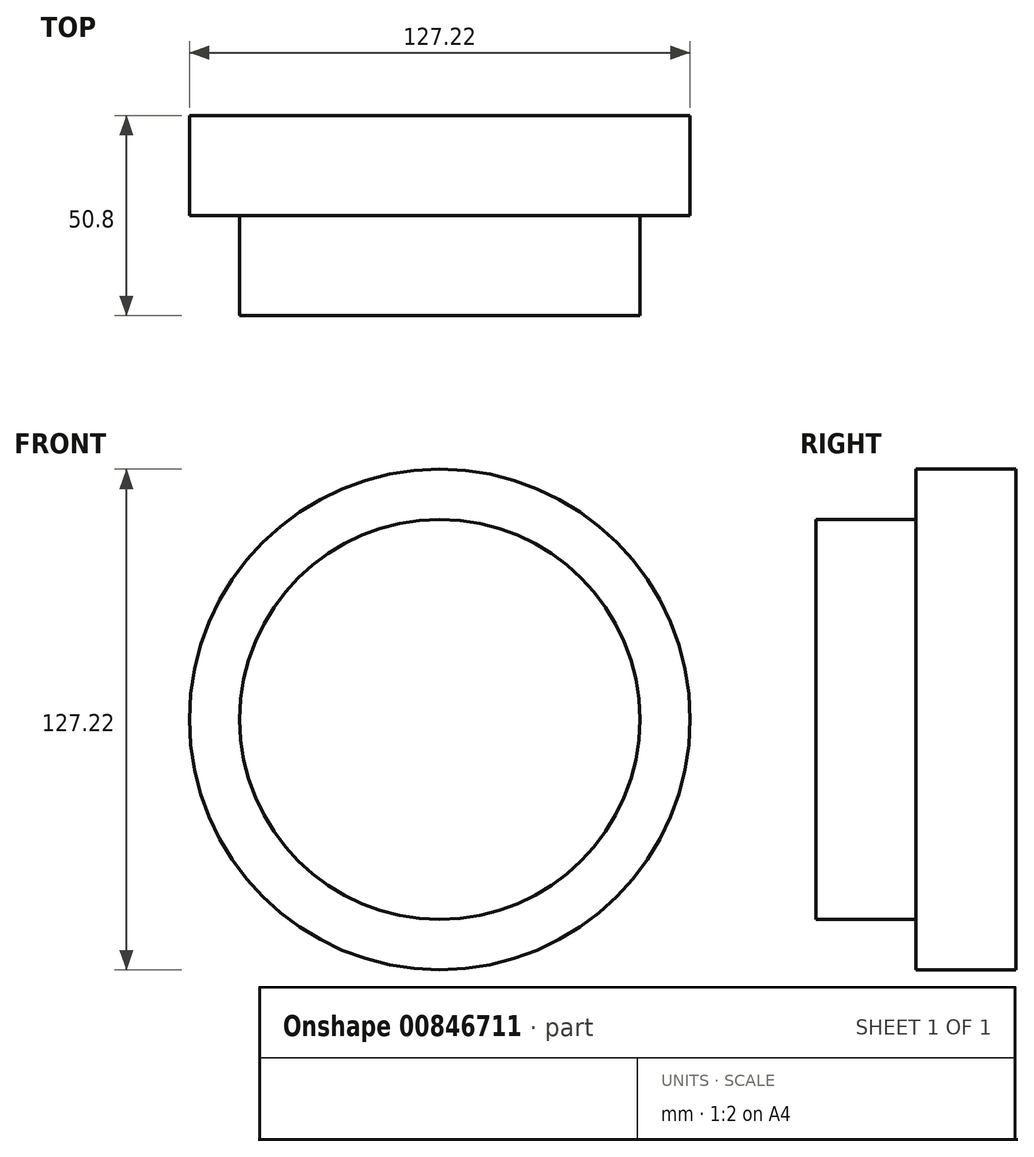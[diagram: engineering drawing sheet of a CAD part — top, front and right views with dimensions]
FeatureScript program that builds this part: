
annotation { "Feature Type Name" : "Feature", "Feature Type Description" : "" }
export const myFeature = defineFeature(function(context is Context, id is Id, definition is map)
    precondition{}
    {
        {
            var Q0;
            Q0=qCreatedBy(makeId("Front.planeOp"),FACE);
            var sketch = newSketch(context, id + "F0", { "sketchPlane" : qUnion([Q0])});
            skCircle(sketch, "E0", {"center": v(0, 0) * mm, "radius": 63.61 * mm});
            skSolve(sketch);
        }
        {
            var Q0;
            Q0=makeQuery(id+"F0.imprint","IMPRINT",FACE,{"disambiguationData":[TD([[makeQuery(id+"F0.imprint","IMPRINT",EDGE,{"derivedFrom":sQuery(id+"F0.wireOp",EDGE,"E0")}),1.0]])]});
            var sketch = newSketch(context, id + "F1", { "sketchPlane" : qUnion([Q0])});
            skCircle(sketch, "E1", {"center": v(0, 0) * mm, "radius": 32.02 * mm});
            skSolve(sketch);
        }
        {
            var Q0;
            Q0=makeQuery(id+"F0.imprint","IMPRINT",FACE,{"disambiguationData":[TD([[makeQuery(id+"F0.imprint","IMPRINT",EDGE,{"derivedFrom":sQuery(id+"F0.wireOp",EDGE,"E0")}),1.0]])]});
            var sketch = newSketch(context, id + "F2", { "sketchPlane" : qUnion([Q0])});
            skLineSegment(sketch, "E2.bottom", {"start": v(-12.32, 12.89) * mm, "end": v(12.7, 12.89) * mm});
            skLineSegment(sketch, "E2.top", {"start": v(-12.32, -14.6) * mm, "end": v(12.7, -14.6) * mm});
            skLineSegment(sketch, "E2.left", {"start": v(-12.32, 12.89) * mm, "end": v(-12.32, -14.6) * mm});
            skLineSegment(sketch, "E2.right", {"start": v(12.7, 12.89) * mm, "end": v(12.7, -14.6) * mm});
            skSolve(sketch);
        }
        {
            var Q0;
            Q0 = qSketchRegion(id + "F2", true);
            extrude(context, id + "F3", {"entities" : qUnion([Q0]), "depth" : 25.4 * mm, "offsetDistance" : 25.4 * mm});
        }
        {
            var Q0;
            Q0=makeQuery(id+"F0.imprint","IMPRINT",FACE,{"disambiguationData":[TD([[makeQuery(id+"F0.imprint","IMPRINT",EDGE,{"derivedFrom":sQuery(id+"F0.wireOp",EDGE,"E0")}),1.0]])]});
            var Q1;
            Q1=makeQuery(id+"F1.imprint","IMPRINT",FACE,{"disambiguationData":[TD([[makeQuery(id+"F1.imprint","IMPRINT",EDGE,{"derivedFrom":sQuery(id+"F1.wireOp",EDGE,"E1")}),1.0]])]});
            extrude(context, id + "F4", {"entities" : qUnion([Q0, Q1]), "operationType" : NewBodyOperationType.ADD, "depth" : 25.4 * mm, "offsetDistance" : 25.4 * mm});
        }
        {
            var Q0;
            Q0=makeQuery(id+"F4.boolean.opBoolean","MERGE",FACE,{"derivedFrom":[makeQuery(id+"F3.opExtrude","CAP_FACE",FACE,{"disambiguationData":[OSD([sQuery(id+"F2.wireOp",EDGE,"E2.bottom"),sQuery(id+"F2.wireOp",EDGE,"E2.top"),sQuery(id+"F2.wireOp",EDGE,"E2.left"),sQuery(id+"F2.wireOp",EDGE,"E2.right")])],"isStart":false}),makeQuery(id+"F4.opExtrude","CAP_FACE",FACE,{"disambiguationData":[OSD([sQuery(id+"F0.wireOp",EDGE,"E0")])],"isStart":false})]});
            var sketch = newSketch(context, id + "F5", { "sketchPlane" : qUnion([Q0])});
            skCircle(sketch, "E3", {"center": v(0, 0) * mm, "radius": 50.83 * mm});
            skSolve(sketch);
        }
        {
            var Q0;
            Q0=makeQuery(id+"F5.imprint","IMPRINT",FACE,{"disambiguationData":[TD([[makeQuery(id+"F5.imprint","IMPRINT",EDGE,{"derivedFrom":sQuery(id+"F5.wireOp",EDGE,"E3")}),1.0]])]});
            extrude(context, id + "F6", {"entities" : qUnion([Q0]), "operationType" : NewBodyOperationType.ADD, "depth" : 25.4 * mm, "offsetDistance" : 25.4 * mm});
        }
    });
